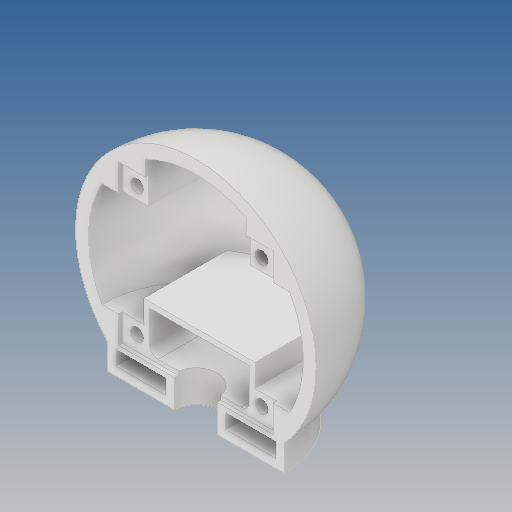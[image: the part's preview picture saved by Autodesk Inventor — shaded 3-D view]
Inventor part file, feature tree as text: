
AUTODESK INVENTOR PART (.ipt)
format: ipt  version: 2020 (Build 240168000, 168)  size: 493,056 bytes
history: native  units: mm
features: other x12, reference x12, sketch x11, extrude x10, fillet x3, projected_geometry x2, revolve x1
ambient origin geometry x8: Origin, YZ Plane, XZ Plane, XY Plane, X Axis, Y Axis, Z Axis, Center Point
bodies: Body1 (feature_tree)
feature tree (51):
  other  "Твердое тело1"
  other  "РабПлоскость1"
  revolve  "Вращение1"
  other  "РабПлоскость2"
  extrude  "Выдавливание1"  Depth=25.0mm
  other  "РабПлоскость3"
  extrude  "Выдавливание2"  Depth=25.0mm
  other  "РабПлоскость4"
  extrude  "Выдавливание3"  Depth=25.0mm
  other  "РабПлоскость5"
  extrude  "Выдавливание5"  Depth=3.0mm
  extrude  "Выдавливание4"  Depth=3.0mm
  extrude  "Выдавливание6"  TaperAngle=180.0deg  [1 undecoded]
  fillet  "Сопряжение1"  Radius=10.0mm
  fillet  "Сопряжение2"  Radius=1.6mm
  other  "РабПлоскость6"
  extrude  "Выдавливание7"  Depth=1.0mm
  extrude  "Выдавливание8"  Depth=1.0mm
  extrude  "Выдавливание9"  Depth=1.0mm
  fillet  "Сопряжение3"  Radius=1.0mm
  extrude  "Выдавливание10"  Depth=1.5mm
  sketch  "Эскиз1"
  sketch  "Эскиз2"
  reference  "Ссылка2"
  reference  "Ссылка3"
  reference  "Ссылка4"
  reference  "Ссылка5"
  sketch  "Эскиз3"
  reference  "Ссылка6"
  reference  "Ссылка7"
  reference  "Ссылка8"
  reference  "Ссылка9"
  sketch  "Эскиз4"
  reference  "Ссылка10"
  reference  "Ссылка11"
  reference  "Ссылка12"
  reference  "Ссылка13"
  sketch  "Эскиз5"
  sketch  "Эскиз6"
  projected_geometry  "Спроецированная петля1"
  sketch  "Эскиз7"
  sketch  "Эскиз8"
  sketch  "Эскиз9"
  projected_geometry  "Спроецированная петля2"
  sketch  "Эскиз10"
  sketch  "Эскиз11"
  other  "<userpath>\Desktop\Робот_Инст\ROBOT_FULL\Camera OV7670.iam"
  other  "Camera OV7670.iam"
  other  "PcbForCamera_1"
  other  "PLS (DS1021-2xN)_DS1021-2x9_5"
  parser-record x1  (decoder bookkeeping rows leaked as tree rows — omitted from the tree; the rows remain in map.json)
note: 1 required parameter value undecoded (feature->parameter linkage not recoverable at this tier; creation-order binding heuristic only, values carry confidence <= 0.55)
note: 1 file-system path scrubbed to <path> (originals preserved in map.json)
